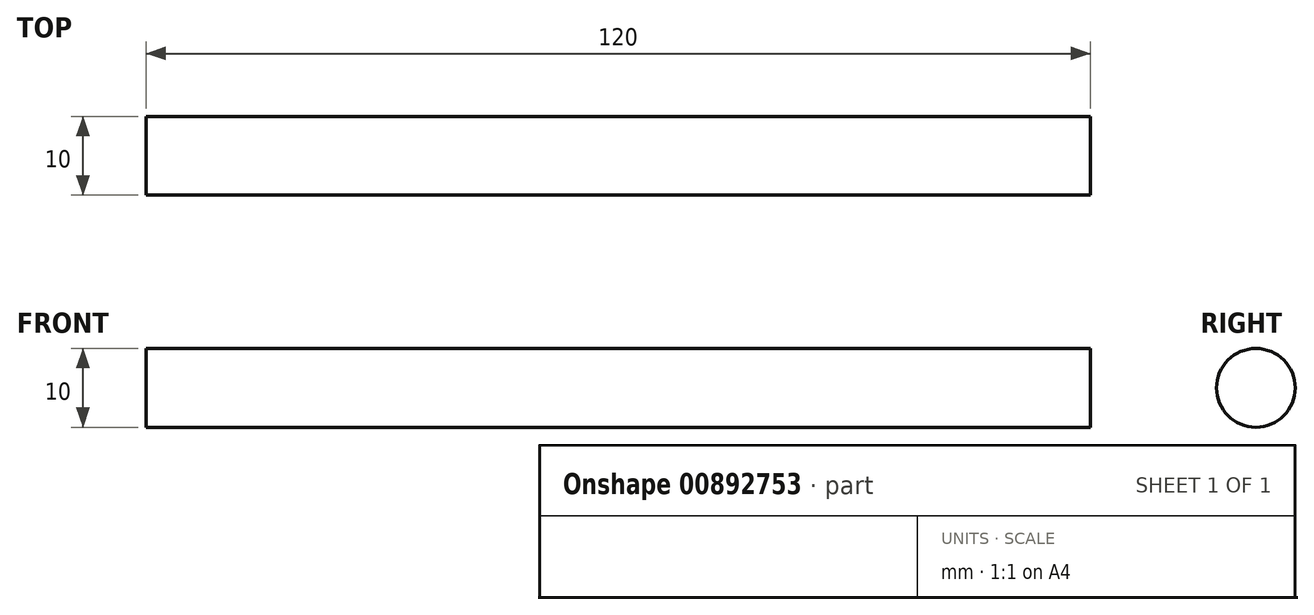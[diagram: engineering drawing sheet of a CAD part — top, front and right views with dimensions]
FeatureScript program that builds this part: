
annotation { "Feature Type Name" : "Feature", "Feature Type Description" : "" }
export const myFeature = defineFeature(function(context is Context, id is Id, definition is map)
    precondition{}
    {
        {
            var Q0;
            Q0=qCreatedBy(makeId("Right.planeOp"),FACE);
            var sketch = newSketch(context, id + "F0", { "sketchPlane" : qUnion([Q0])});
            skCircle(sketch, "E0", {"center": v(0, 0) * mm, "radius": 5 * mm});
            skSolve(sketch);
        }
        {
            var Q0;
            Q0=makeQuery(id+"F0.imprint","IMPRINT",FACE,{"disambiguationData":[TD([[makeQuery(id+"F0.imprint","IMPRINT",EDGE,{"derivedFrom":sQuery(id+"F0.wireOp",EDGE,"E0")}),1.0]])]});
            extrude(context, id + "F1", {"entities" : qUnion([Q0]), "depth" : 120 * mm, "offsetDistance" : 25 * mm});
        }
    });
